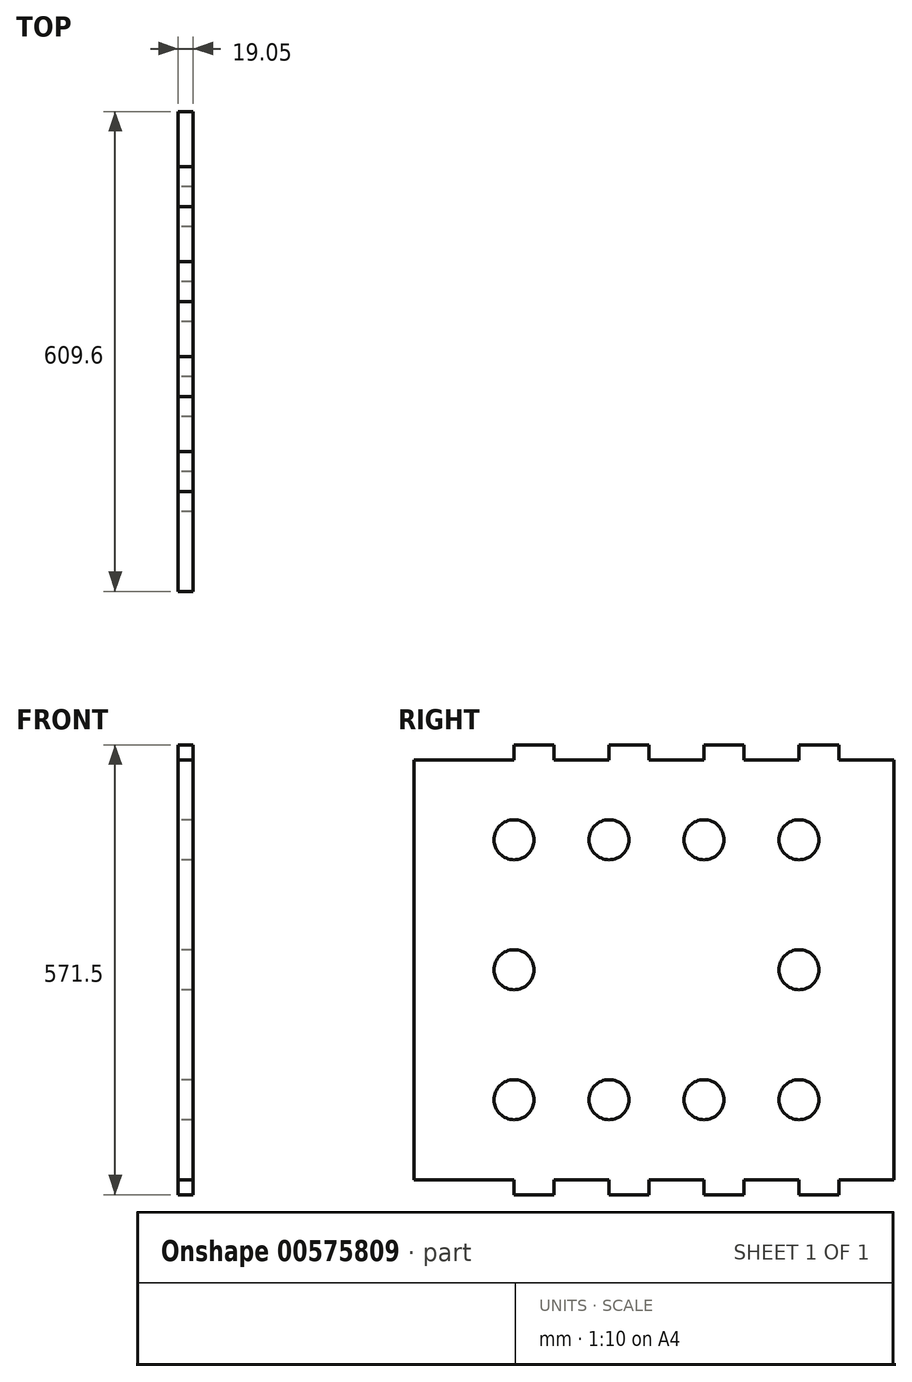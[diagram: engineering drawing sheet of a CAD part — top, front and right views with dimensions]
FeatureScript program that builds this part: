
annotation { "Feature Type Name" : "Feature", "Feature Type Description" : "" }
export const myFeature = defineFeature(function(context is Context, id is Id, definition is map)
    precondition{}
    {
        {
            var Q0;
            Q0=qCreatedBy(makeId("Top.planeOp"),FACE);
            var sketch = newSketch(context, id + "F0", { "sketchPlane" : qUnion([Q0])});
            skLineSegment(sketch, "E0.bottom", {"start": v(0, 0) * mm, "end": v(19.05, 0) * mm});
            skLineSegment(sketch, "E0.top", {"start": v(0, 609.6) * mm, "end": v(19.05, 609.6) * mm});
            skLineSegment(sketch, "E0.left", {"start": v(0, 0) * mm, "end": v(0, 609.6) * mm});
            skLineSegment(sketch, "E0.right", {"start": v(19.05, 0) * mm, "end": v(19.05, 609.6) * mm});
            skSolve(sketch);
        }
        {
            var Q0;
            Q0 = qSketchRegion(id + "F0", true);
            extrude(context, id + "F1", {"entities" : qUnion([Q0]), "depth" : 533.4 * mm, "offsetDistance" : 25.4 * mm});
        }
        {
            var Q0;
            Q0=makeQuery(id+"F1.opExtrude","CAP_FACE",FACE,{"disambiguationData":[OSD([sQuery(id+"F0.wireOp",EDGE,"E0.bottom"),sQuery(id+"F0.wireOp",EDGE,"E0.top"),sQuery(id+"F0.wireOp",EDGE,"E0.left"),sQuery(id+"F0.wireOp",EDGE,"E0.right")])],"isStart":true});
            var sketch = newSketch(context, id + "F2", { "sketchPlane" : qUnion([Q0])});
            skLineSegment(sketch, "E1.bottom", {"start": v(0, -127) * mm, "end": v(19.05, -127) * mm});
            skLineSegment(sketch, "E1.top", {"start": v(0, -177.8) * mm, "end": v(19.05, -177.8) * mm});
            skLineSegment(sketch, "E1.left", {"start": v(0, -127) * mm, "end": v(0, -177.8) * mm});
            skLineSegment(sketch, "E1.right", {"start": v(19.05, -127) * mm, "end": v(19.05, -177.8) * mm});
            skLineSegment(sketch, "E2.bottom", {"start": v(0, -247.65) * mm, "end": v(19.05, -247.65) * mm});
            skLineSegment(sketch, "E2.top", {"start": v(0, -298.45) * mm, "end": v(19.05, -298.45) * mm});
            skLineSegment(sketch, "E2.left", {"start": v(0, -247.65) * mm, "end": v(0, -298.45) * mm});
            skLineSegment(sketch, "E2.right", {"start": v(19.05, -247.65) * mm, "end": v(19.05, -298.45) * mm});
            skLineSegment(sketch, "E3.bottom", {"start": v(0, -368.3) * mm, "end": v(19.05, -368.3) * mm});
            skLineSegment(sketch, "E3.top", {"start": v(0, -419.1) * mm, "end": v(19.05, -419.1) * mm});
            skLineSegment(sketch, "E3.left", {"start": v(0, -368.3) * mm, "end": v(0, -419.1) * mm});
            skLineSegment(sketch, "E3.right", {"start": v(19.05, -368.3) * mm, "end": v(19.05, -419.1) * mm});
            skLineSegment(sketch, "E4.bottom", {"start": v(0, -488.95) * mm, "end": v(19.05, -488.95) * mm});
            skLineSegment(sketch, "E4.top", {"start": v(0, -539.75) * mm, "end": v(19.05, -539.75) * mm});
            skLineSegment(sketch, "E4.left", {"start": v(0, -488.95) * mm, "end": v(0, -539.75) * mm});
            skLineSegment(sketch, "E4.right", {"start": v(19.05, -488.95) * mm, "end": v(19.05, -539.75) * mm});
            skSolve(sketch);
        }
        {
            var Q0;
            Q0 = qSketchRegion(id + "F2", true);
            extrude(context, id + "F3", {"entities" : qUnion([Q0]), "operationType" : NewBodyOperationType.ADD, "depth" : 19.05 * mm, "offsetDistance" : 25.4 * mm});
        }
        {
            var Q0;
            Q0=makeQuery(id+"F1.opExtrude","CAP_FACE",FACE,{"disambiguationData":[OSD([sQuery(id+"F0.wireOp",EDGE,"E0.bottom"),sQuery(id+"F0.wireOp",EDGE,"E0.top"),sQuery(id+"F0.wireOp",EDGE,"E0.left"),sQuery(id+"F0.wireOp",EDGE,"E0.right")])],"isStart":false});
            var sketch = newSketch(context, id + "F4", { "sketchPlane" : qUnion([Q0])});
            skLineSegment(sketch, "E5.bottom", {"start": v(0, 539.75) * mm, "end": v(19.05, 539.75) * mm});
            skLineSegment(sketch, "E5.top", {"start": v(0, 488.95) * mm, "end": v(19.05, 488.95) * mm});
            skLineSegment(sketch, "E5.left", {"start": v(0, 539.75) * mm, "end": v(0, 488.95) * mm});
            skLineSegment(sketch, "E5.right", {"start": v(19.05, 539.75) * mm, "end": v(19.05, 488.95) * mm});
            skLineSegment(sketch, "E6.bottom", {"start": v(0, 419.1) * mm, "end": v(19.05, 419.1) * mm});
            skLineSegment(sketch, "E6.top", {"start": v(0, 368.3) * mm, "end": v(19.05, 368.3) * mm});
            skLineSegment(sketch, "E6.left", {"start": v(0, 419.1) * mm, "end": v(0, 368.3) * mm});
            skLineSegment(sketch, "E6.right", {"start": v(19.05, 419.1) * mm, "end": v(19.05, 368.3) * mm});
            skLineSegment(sketch, "E7.bottom", {"start": v(0, 298.45) * mm, "end": v(19.05, 298.45) * mm});
            skLineSegment(sketch, "E7.top", {"start": v(0, 247.65) * mm, "end": v(19.05, 247.65) * mm});
            skLineSegment(sketch, "E7.left", {"start": v(0, 298.45) * mm, "end": v(0, 247.65) * mm});
            skLineSegment(sketch, "E7.right", {"start": v(19.05, 298.45) * mm, "end": v(19.05, 247.65) * mm});
            skLineSegment(sketch, "E8.bottom", {"start": v(0, 177.8) * mm, "end": v(19.05, 177.8) * mm});
            skLineSegment(sketch, "E8.top", {"start": v(0, 127) * mm, "end": v(19.05, 127) * mm});
            skLineSegment(sketch, "E8.left", {"start": v(0, 177.8) * mm, "end": v(0, 127) * mm});
            skLineSegment(sketch, "E8.right", {"start": v(19.05, 177.8) * mm, "end": v(19.05, 127) * mm});
            skSolve(sketch);
        }
        {
            var Q0;
            Q0 = qSketchRegion(id + "F4", true);
            extrude(context, id + "F5", {"entities" : qUnion([Q0]), "operationType" : NewBodyOperationType.ADD, "depth" : 19.05 * mm, "offsetDistance" : 25.4 * mm});
        }
        {
            var Q0;
            Q0=makeQuery(id+"F5.boolean.opBoolean","MERGE",FACE,{"derivedFrom":[makeQuery(id+"F3.boolean.opBoolean","MERGE",FACE,{"derivedFrom":[makeQuery(id+"F1.opExtrude","SWEPT_FACE",FACE,{"disambiguationData":[OSD([sQuery(id+"F0.wireOp",EDGE,"E0.left")])]}),makeQuery(id+"F3.opExtrude","SWEPT_FACE",FACE,{"disambiguationData":[OSD([sQuery(id+"F2.wireOp",EDGE,"E1.left")])]}),makeQuery(id+"F3.opExtrude","SWEPT_FACE",FACE,{"disambiguationData":[OSD([sQuery(id+"F2.wireOp",EDGE,"E2.left")])]}),makeQuery(id+"F3.opExtrude","SWEPT_FACE",FACE,{"disambiguationData":[OSD([sQuery(id+"F2.wireOp",EDGE,"E3.left")])]}),makeQuery(id+"F3.opExtrude","SWEPT_FACE",FACE,{"disambiguationData":[OSD([sQuery(id+"F2.wireOp",EDGE,"E4.left")])]})]}),makeQuery(id+"F5.opExtrude","SWEPT_FACE",FACE,{"disambiguationData":[OSD([sQuery(id+"F4.wireOp",EDGE,"E5.left")])]}),makeQuery(id+"F5.opExtrude","SWEPT_FACE",FACE,{"disambiguationData":[OSD([sQuery(id+"F4.wireOp",EDGE,"E6.left")])]}),makeQuery(id+"F5.opExtrude","SWEPT_FACE",FACE,{"disambiguationData":[OSD([sQuery(id+"F4.wireOp",EDGE,"E7.left")])]}),makeQuery(id+"F5.opExtrude","SWEPT_FACE",FACE,{"disambiguationData":[OSD([sQuery(id+"F4.wireOp",EDGE,"E8.left")])]})]});
            var sketch = newSketch(context, id + "F6", { "sketchPlane" : qUnion([Q0])});
            skCircle(sketch, "E9", {"center": v(-488.95, 101.6) * mm, "radius": 25.4 * mm});
            skCircle(sketch, "E10", {"center": v(-368.3, 101.6) * mm, "radius": 25.4 * mm});
            skCircle(sketch, "E11", {"center": v(-247.65, 101.6) * mm, "radius": 25.4 * mm});
            skCircle(sketch, "E12", {"center": v(-127, 101.6) * mm, "radius": 25.4 * mm});
            skCircle(sketch, "E13", {"center": v(-488.95, 431.8) * mm, "radius": 25.4 * mm});
            skCircle(sketch, "E14", {"center": v(-368.3, 431.8) * mm, "radius": 25.4 * mm});
            skCircle(sketch, "E15", {"center": v(-247.65, 431.8) * mm, "radius": 25.4 * mm});
            skCircle(sketch, "E16", {"center": v(-127, 431.8) * mm, "radius": 25.4 * mm});
            skCircle(sketch, "E17", {"center": v(-127, 266.7) * mm, "radius": 25.4 * mm});
            skPoint(sketch, "E17.centerSnap0", {"position": v(0, 266.7) * mm});
            skCircle(sketch, "E18", {"center": v(-488.95, 266.7) * mm, "radius": 25.4 * mm});
            skPoint(sketch, "E18.centerSnap0", {"position": v(-609.6, 266.7) * mm});
            skSolve(sketch);
        }
        {
            var Q0;
            Q0 = qSketchRegion(id + "F6", true);
            extrude(context, id + "F7", {"entities" : qUnion([Q0]), "operationType" : NewBodyOperationType.REMOVE, "oppositeDirection" : true, "depth" : 19.05 * mm, "offsetDistance" : 25.4 * mm});
        }
    });
